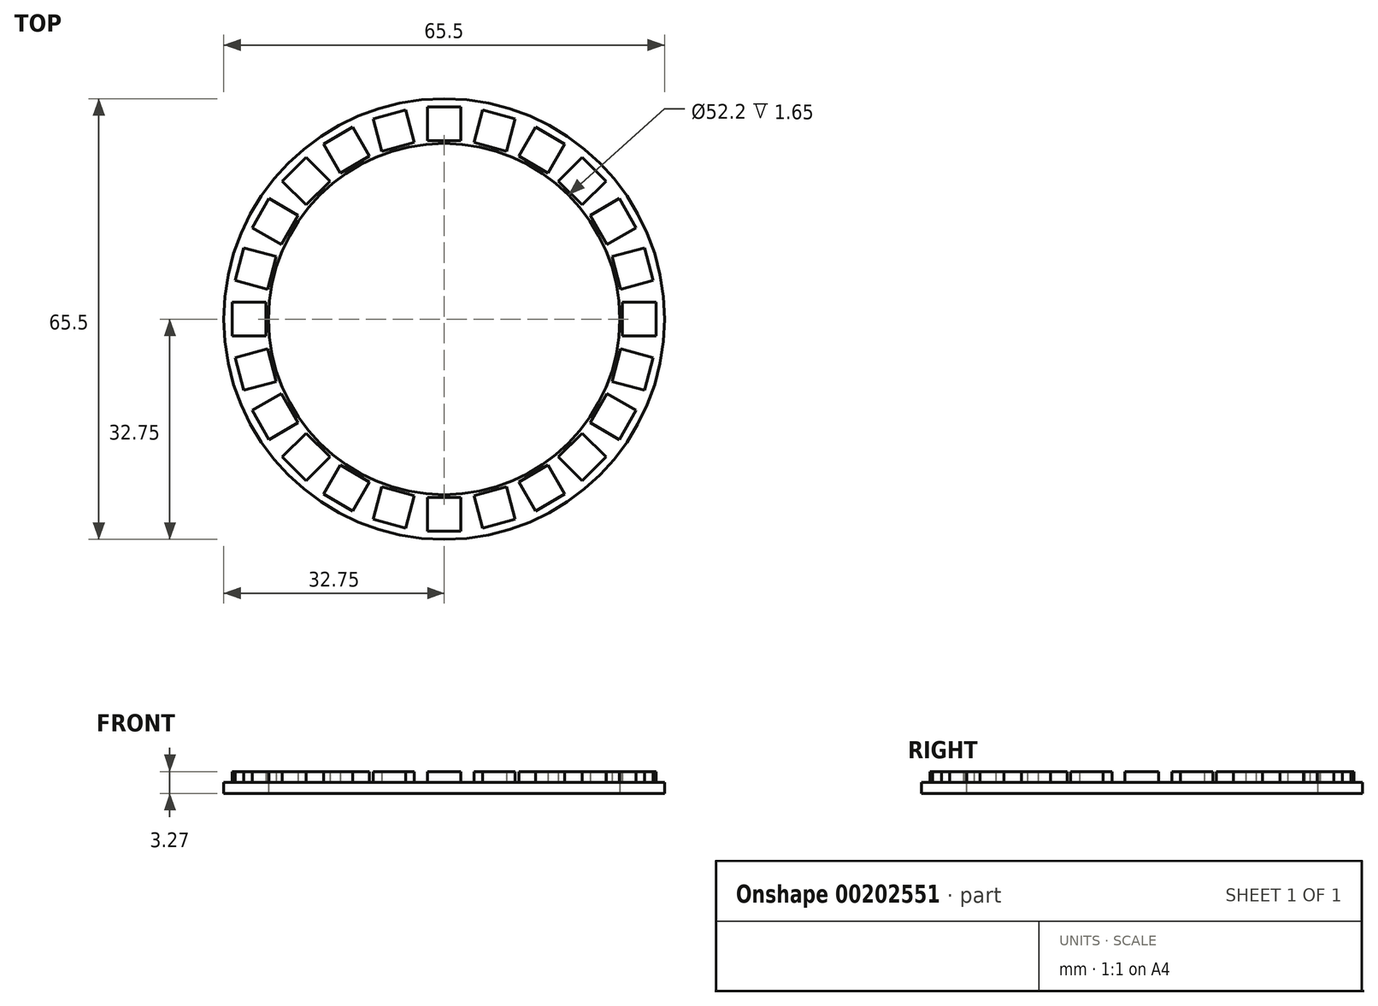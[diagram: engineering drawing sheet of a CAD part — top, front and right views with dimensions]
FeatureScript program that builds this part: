
annotation { "Feature Type Name" : "Feature", "Feature Type Description" : "" }
export const myFeature = defineFeature(function(context is Context, id is Id, definition is map)
    precondition{}
    {
        {
            var Q0;
            Q0=qCreatedBy(makeId("Top.planeOp"),FACE);
            var sketch = newSketch(context, id + "F0", { "sketchPlane" : qUnion([Q0])});
            skCircle(sketch, "E0", {"center": v(0, 0) * mm, "radius": 32.75 * mm});
            skCircle(sketch, "E1", {"center": v(0, 0) * mm, "radius": 26.1 * mm});
            skSolve(sketch);
        }
        {
            var Q0;
            Q0=qSketchRegion(id+"F0",true);
            extrude(context, id + "F1", {"entities" : qUnion([Q0]), "depth" : 1.65 * mm});
        }
        {
            var Q0;
            Q0=makeQuery(id+"F1.opExtrude","CAP_FACE",FACE,{"disambiguationData":[OSD([sQuery(id+"F0.wireOp",EDGE,"E0"),sQuery(id+"F0.wireOp",EDGE,"E1")])],"isStart":false});
            var sketch = newSketch(context, id + "F2", { "sketchPlane" : qUnion([Q0])});
            skLineSegment(sketch, "E2.bottom", {"start": v(2.5, -26.5) * mm, "end": v(-2.5, -26.5) * mm});
            skLineSegment(sketch, "E2.top", {"start": v(2.5, -31.5) * mm, "end": v(-2.5, -31.5) * mm});
            skLineSegment(sketch, "E2.left", {"start": v(2.5, -26.5) * mm, "end": v(2.5, -31.5) * mm});
            skLineSegment(sketch, "E2.right", {"start": v(-2.5, -26.5) * mm, "end": v(-2.5, -31.5) * mm});
            skPoint(sketch, "E2.middle", {"position": v(0, -29) * mm});
            skSolve(sketch);
        }
        {
            var Q0;
            Q0=makeQuery(id+"F2.imprint","IMPRINT",FACE,{"disambiguationData":[TD([[makeQuery(id+"F2.imprint","IMPRINT",EDGE,{"derivedFrom":sQuery(id+"F2.wireOp",EDGE,"E2.bottom")}),1.0]])]});
            extrude(context, id + "F3", {"entities" : qUnion([Q0]), "depth" : 1.62 * mm});
        }
        {
            var Q0;
            Q0=makeQuery(id+"F3.opExtrude","SWEPT_BODY",BODY,{"disambiguationData":[OSD([sQuery(id+"F2.wireOp",EDGE,"E2.bottom"),sQuery(id+"F2.wireOp",EDGE,"E2.top"),sQuery(id+"F2.wireOp",EDGE,"E2.left"),sQuery(id+"F2.wireOp",EDGE,"E2.right")])]});
            var Q1;
            Q1=makeQuery(id+"F1.opExtrude","CAP_EDGE",EDGE,{"disambiguationData":[OSD([sQuery(id+"F0.wireOp",EDGE,"E0")])],"isStart":false});
            circularPattern(context, id + "F4", {"entities" : qUnion([Q0]), "axis" : qUnion([Q1]), "angle" : 360 * degree, "instanceCount" : 24, "equalSpace" : true});
        }
    });
